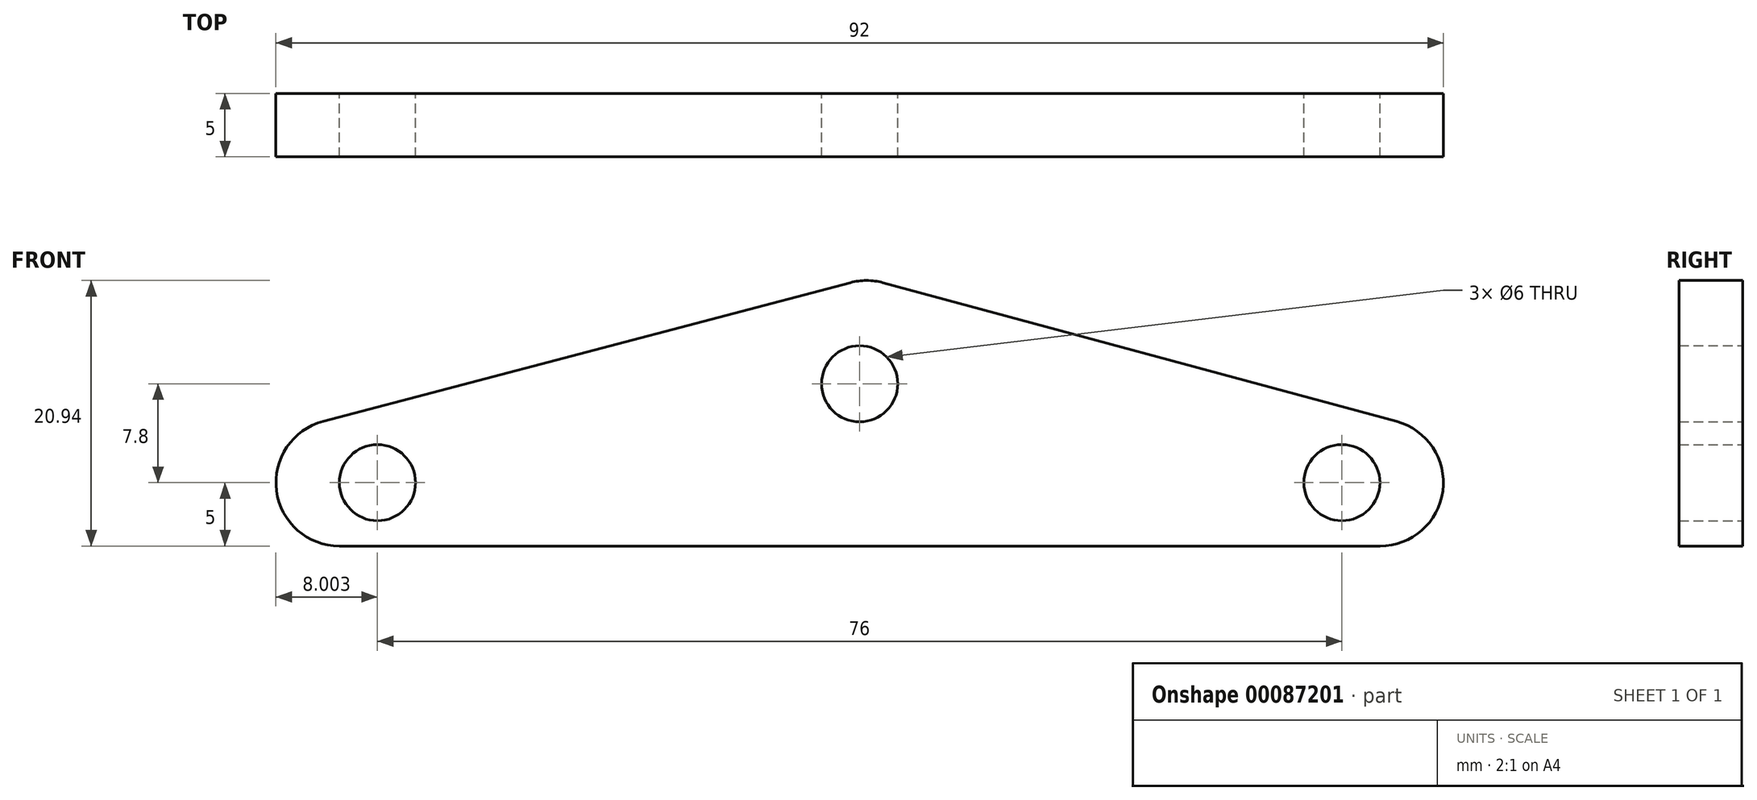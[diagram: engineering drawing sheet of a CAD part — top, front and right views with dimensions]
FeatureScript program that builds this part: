
annotation { "Feature Type Name" : "Feature", "Feature Type Description" : "" }
export const myFeature = defineFeature(function(context is Context, id is Id, definition is map)
    precondition{}
    {
        {
            var Q0;
            Q0=qCreatedBy(makeId("Front.planeOp"),FACE);
            var sketch = newSketch(context, id + "F0", { "sketchPlane" : qUnion([Q0])});
            skLineSegment(sketch, "E0", {"start": v(-17.42, 0) * mm, "end": v(20.58, 0) * mm, "construction": true});
            skLineSegment(sketch, "E1", {"start": v(20.58, 0) * mm, "end": v(20.58, 7.8) * mm, "construction": true});
            skCircle(sketch, "E2", {"center": v(20.58, 7.8) * mm, "radius": 3 * mm});
            skCircle(sketch, "E3", {"center": v(-17.42, 0) * mm, "radius": 3 * mm});
            skLineSegment(sketch, "E4.MirrorCS", {"start": v(58.58, 0) * mm, "end": v(20.58, 0) * mm, "construction": true});
            skCircle(sketch, "E5.MirrorC", {"center": v(58.58, 0) * mm, "radius": 3 * mm});
            skLineSegment(sketch, "E6", {"start": v(-21.7, 4.83) * mm, "end": v(19.83, 15.78) * mm});
            skLineSegment(sketch, "E7", {"start": v(22.41, 15.77) * mm, "end": v(62.89, 4.83) * mm});
            skLineSegment(sketch, "E8", {"start": v(-20.42, -5) * mm, "end": v(61.58, -5) * mm});
            skPoint(sketch, "E9.visualSharp", {"position": v(-59.02, -5) * mm});
            skArc(sketch, "E9.filletArc", {"start": v(-21.7, 4.83) * mm, "mid": v(-25.38, -0.64) * mm, "end": v(-20.42, -5) * mm});
            skPoint(sketch, "E10.visualSharp", {"position": v(99.24, -5) * mm});
            skArc(sketch, "E10.filletArc", {"start": v(61.58, -5) * mm, "mid": v(66.54, -0.66) * mm, "end": v(62.89, 4.83) * mm});
            skPoint(sketch, "E11.visualSharp", {"position": v(21.12, 16.12) * mm});
            skArc(sketch, "E11.filletArc", {"start": v(22.41, 15.77) * mm, "mid": v(21.12, 15.94) * mm, "end": v(19.83, 15.78) * mm});
            skSolve(sketch);
        }
        {
            var Q0;
            Q0 = qSketchRegion(id + "F0", true);
            extrude(context, id + "F1", {"entities" : qUnion([Q0]), "depth" : 5 * mm});
        }
    });
